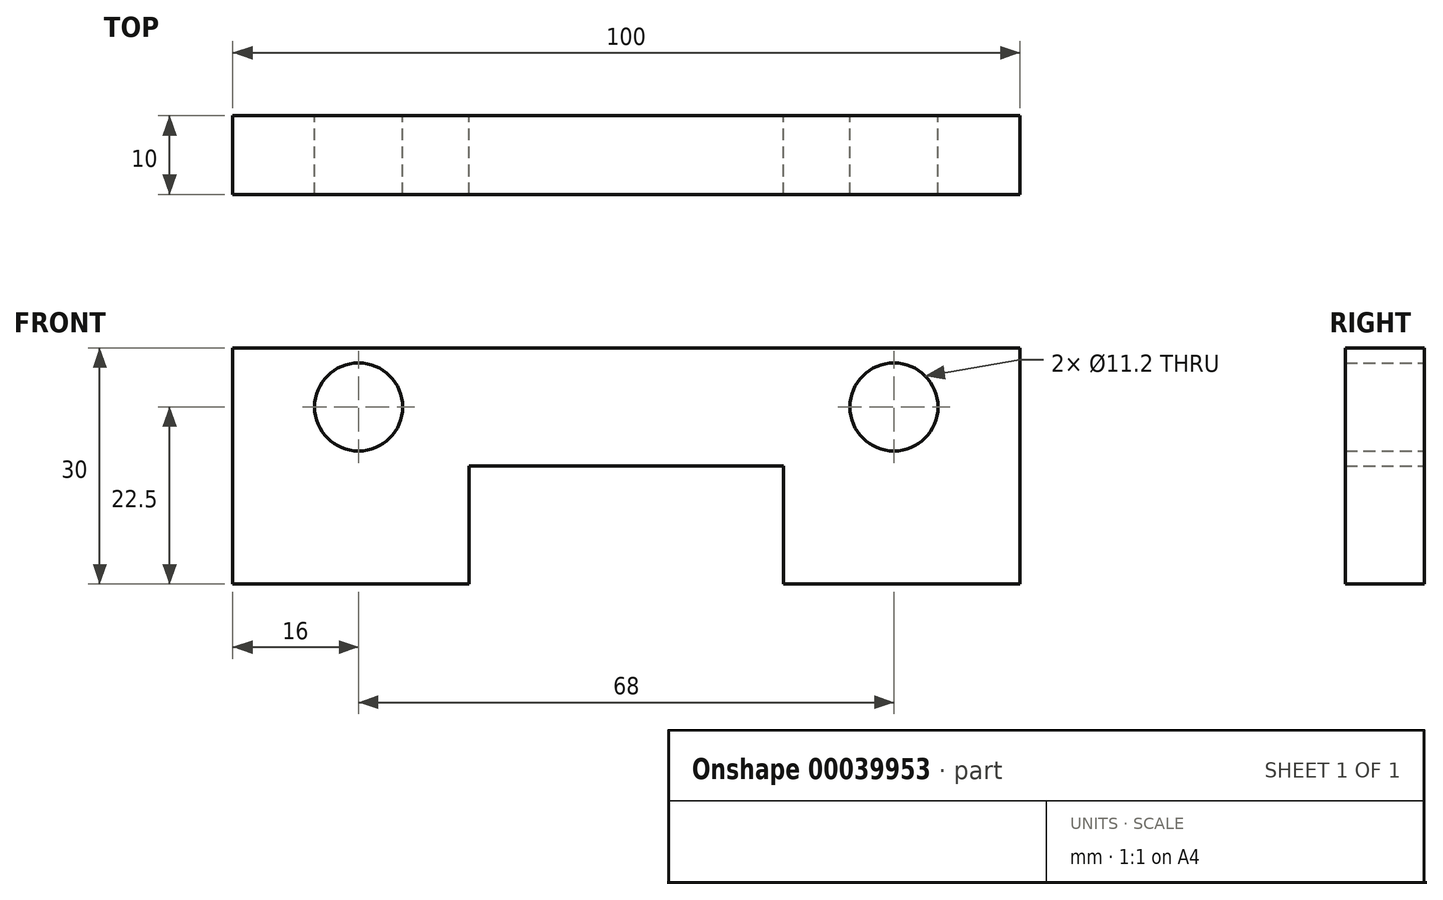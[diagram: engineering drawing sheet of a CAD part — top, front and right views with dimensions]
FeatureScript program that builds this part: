
annotation { "Feature Type Name" : "Feature", "Feature Type Description" : "" }
export const myFeature = defineFeature(function(context is Context, id is Id, definition is map)
    precondition{}
    {
        {
            var Q0;
            Q0=qCreatedBy(makeId("Front.planeOp"),FACE);
            var sketch = newSketch(context, id + "F0", { "sketchPlane" : qUnion([Q0])});
            skLineSegment(sketch, "E0.rect.bottom", {"start": v(-50, 7.5) * mm, "end": v(50, 7.5) * mm});
            skLineSegment(sketch, "E0.rect.top", {"start": v(-50, -7.5) * mm, "end": v(50, -7.5) * mm});
            skLineSegment(sketch, "E0.rect.left", {"start": v(-50, 7.5) * mm, "end": v(-50, -7.5) * mm});
            skLineSegment(sketch, "E0.rect.right", {"start": v(50, 7.5) * mm, "end": v(50, -7.5) * mm});
            skPoint(sketch, "E0.rect.middle", {"position": v(0, 0) * mm});
            skLineSegment(sketch, "E1.bottom", {"start": v(-50, -7.5) * mm, "end": v(-20, -7.5) * mm});
            skLineSegment(sketch, "E1.top", {"start": v(-50, -22.5) * mm, "end": v(-20, -22.5) * mm});
            skLineSegment(sketch, "E1.left", {"start": v(-50, -7.5) * mm, "end": v(-50, -22.5) * mm});
            skLineSegment(sketch, "E1.right", {"start": v(-20, -7.5) * mm, "end": v(-20, -22.5) * mm});
            skLineSegment(sketch, "E2.bottom", {"start": v(50, -7.5) * mm, "end": v(20, -7.5) * mm});
            skLineSegment(sketch, "E2.top", {"start": v(50, -22.5) * mm, "end": v(20, -22.5) * mm});
            skLineSegment(sketch, "E2.left", {"start": v(50, -7.5) * mm, "end": v(50, -22.5) * mm});
            skLineSegment(sketch, "E2.right", {"start": v(20, -7.5) * mm, "end": v(20, -22.5) * mm});
            skCircle(sketch, "E3", {"center": v(-34, 0) * mm, "radius": 5.6 * mm});
            skCircle(sketch, "E4", {"center": v(34, 0) * mm, "radius": 5.6 * mm});
            skSolve(sketch);
        }
        {
            var Q0;
            Q0 = qSketchRegion(id + "F0", true);
            extrude(context, id + "F1", {"entities" : qUnion([Q0]), "endBound" : BoundingType.SYMMETRIC, "depth" : 10 * mm});
        }
    });
